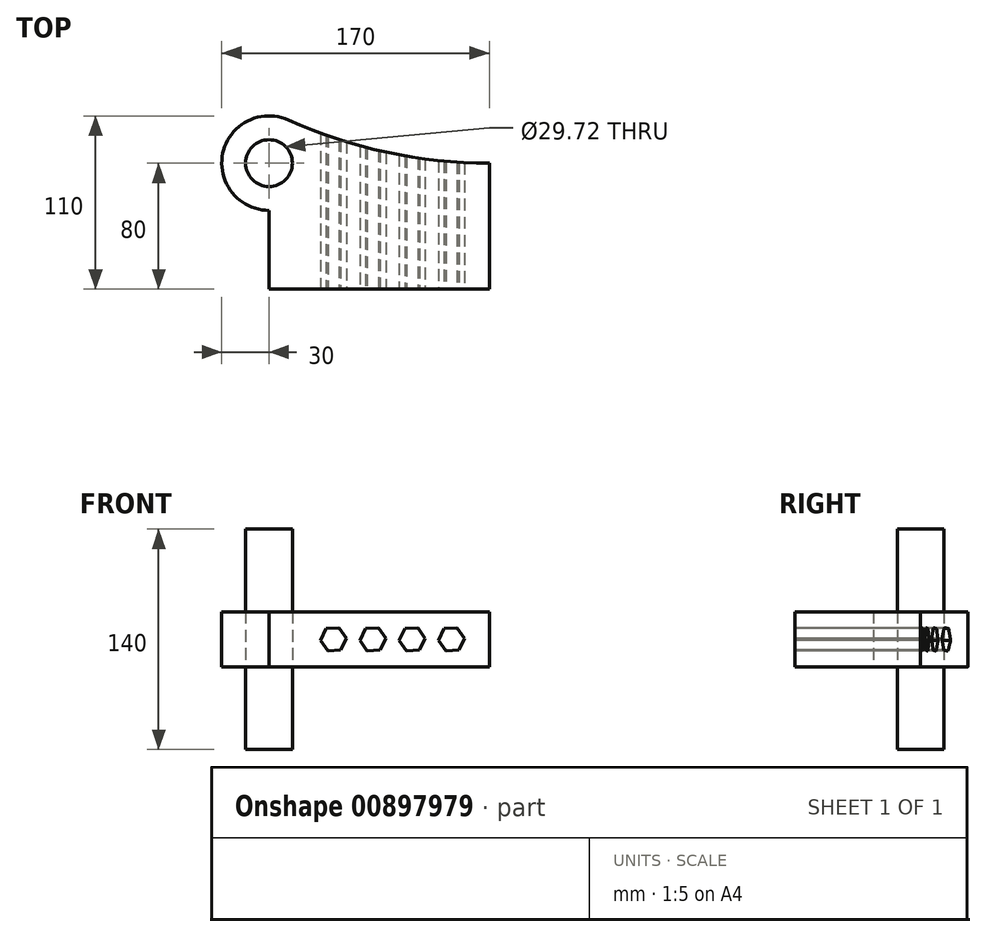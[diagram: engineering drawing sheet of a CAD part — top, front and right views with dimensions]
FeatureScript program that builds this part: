
annotation { "Feature Type Name" : "Feature", "Feature Type Description" : "" }
export const myFeature = defineFeature(function(context is Context, id is Id, definition is map)
    precondition{}
    {
        {
            var Q0;
            Q0=qCreatedBy(makeId("Top.planeOp"),FACE);
            var sketch = newSketch(context, id + "F0", { "sketchPlane" : qUnion([Q0])});
            skLineSegment(sketch, "E0.bottom", {"start": v(70, -40) * mm, "end": v(-70, -40) * mm});
            skLineSegment(sketch, "E0.top", {"start": v(70, 40) * mm, "end": v(-70, 40) * mm});
            skLineSegment(sketch, "E0.left", {"start": v(70, -40) * mm, "end": v(70, 40) * mm});
            skLineSegment(sketch, "E0.right", {"start": v(-70, -40) * mm, "end": v(-70, 40) * mm});
            skPoint(sketch, "E0.middle", {"position": v(0, 0) * mm});
            skCircle(sketch, "E1", {"center": v(-70, 40) * mm, "radius": 30 * mm});
            skArc(sketch, "E2", {"start": v(-57.7, 67.37) * mm, "mid": v(4.7, 46.92) * mm, "end": v(70, 40) * mm});
            skCircle(sketch, "E3", {"center": v(-70, 40) * mm, "radius": 14.86 * mm});
            skSolve(sketch);
        }
        {
            var Q0;
            Q0 = qSketchRegion(id + "F0", true);
            extrude(context, id + "F1", {"entities" : qUnion([Q0]), "endBound" : BoundingType.SYMMETRIC, "depth" : 35 * mm, "offsetDistance" : 25 * mm});
        }
        {
            var Q0;
            {var subQ0=sQuery(id+"F0.wireOp",EDGE,"E0.right");var subQ1=sQuery(id+"F0.wireOp",EDGE,"E0.top");var subQ2=makeQuery(id+"F0.imprint","INTERSECT",VERTEX,{"derivedFrom":[subQ1,subQ0]});Q0=makeQuery(id+"F0.imprint","IMPRINT",FACE,{"disambiguationData":[TD([[makeQuery(id+"F0.imprint","IMPRINT",EDGE,{"disambiguationData":[TD([[subQ2,1.0]])],"derivedFrom":subQ1}),-1.0]])]});}
            var Q1;
            {var subQ0=sQuery(id+"F0.wireOp",EDGE,"E0.right");var subQ1=sQuery(id+"F0.wireOp",EDGE,"E0.top");var subQ2=makeQuery(id+"F0.imprint","INTERSECT",VERTEX,{"derivedFrom":[subQ1,subQ0]});Q1=makeQuery(id+"F0.imprint","IMPRINT",FACE,{"disambiguationData":[TD([[makeQuery(id+"F0.imprint","IMPRINT",EDGE,{"disambiguationData":[TD([[subQ2,1.0]])],"derivedFrom":subQ1}),1.0]])]});}
            extrude(context, id + "F2", {"entities" : qUnion([Q0, Q1]), "endBound" : BoundingType.SYMMETRIC, "depth" : 140 * mm, "offsetDistance" : 25 * mm});
        }
        {
            var Q0;
            Q0=makeQuery(id+"F1.opExtrude","SWEPT_FACE",FACE,{"disambiguationData":[OSD([sQuery(id+"F0.wireOp",EDGE,"E0.bottom")])]});
            var sketch = newSketch(context, id + "F3", { "sketchPlane" : qUnion([Q0])});
            skCircle(sketch, "E4.cCircle", {"center": v(-29.05, 0) * mm, "radius": 8.24 * mm, "construction": true});
            skLineSegment(sketch, "E4.0", {"start": v(-24.41, -6.81) * mm, "end": v(-32.63, -7.42) * mm});
            skLineSegment(sketch, "E4.1", {"start": v(-32.63, -7.42) * mm, "end": v(-37.27, -0.61) * mm});
            skLineSegment(sketch, "E4.2", {"start": v(-37.27, -0.61) * mm, "end": v(-33.69, 6.81) * mm});
            skLineSegment(sketch, "E4.3", {"start": v(-33.69, 6.81) * mm, "end": v(-25.47, 7.42) * mm});
            skLineSegment(sketch, "E4.4", {"start": v(-25.47, 7.42) * mm, "end": v(-20.83, 0.61) * mm});
            skLineSegment(sketch, "E4.5", {"start": v(-20.83, 0.61) * mm, "end": v(-24.41, -6.81) * mm});
            skLineSegment(sketch, "E5.1.0.0", {"start": v(-8.69, 6.81) * mm, "end": v(-0.47, 7.42) * mm});
            skLineSegment(sketch, "E5.1.0.1", {"start": v(-12.27, -0.61) * mm, "end": v(-8.69, 6.81) * mm});
            skLineSegment(sketch, "E5.1.0.2", {"start": v(-7.63, -7.42) * mm, "end": v(-12.27, -0.61) * mm});
            skLineSegment(sketch, "E5.1.0.3", {"start": v(0.59, -6.81) * mm, "end": v(-7.63, -7.42) * mm});
            skLineSegment(sketch, "E5.1.0.4", {"start": v(4.17, 0.61) * mm, "end": v(0.59, -6.81) * mm});
            skLineSegment(sketch, "E5.1.0.5", {"start": v(-0.47, 7.42) * mm, "end": v(4.17, 0.61) * mm});
            skLineSegment(sketch, "E5.2.0.0", {"start": v(16.31, 6.81) * mm, "end": v(24.53, 7.42) * mm});
            skLineSegment(sketch, "E5.2.0.1", {"start": v(12.73, -0.61) * mm, "end": v(16.31, 6.81) * mm});
            skLineSegment(sketch, "E5.2.0.2", {"start": v(17.37, -7.42) * mm, "end": v(12.73, -0.61) * mm});
            skLineSegment(sketch, "E5.2.0.3", {"start": v(25.59, -6.81) * mm, "end": v(17.37, -7.42) * mm});
            skLineSegment(sketch, "E5.2.0.4", {"start": v(29.17, 0.61) * mm, "end": v(25.59, -6.81) * mm});
            skLineSegment(sketch, "E5.2.0.5", {"start": v(24.53, 7.42) * mm, "end": v(29.17, 0.61) * mm});
            skLineSegment(sketch, "E5.3.0.0", {"start": v(41.31, 6.81) * mm, "end": v(49.53, 7.42) * mm});
            skLineSegment(sketch, "E5.3.0.1", {"start": v(37.73, -0.61) * mm, "end": v(41.31, 6.81) * mm});
            skLineSegment(sketch, "E5.3.0.2", {"start": v(42.37, -7.42) * mm, "end": v(37.73, -0.61) * mm});
            skLineSegment(sketch, "E5.3.0.3", {"start": v(50.59, -6.81) * mm, "end": v(42.37, -7.42) * mm});
            skLineSegment(sketch, "E5.3.0.4", {"start": v(54.17, 0.61) * mm, "end": v(50.59, -6.81) * mm});
            skLineSegment(sketch, "E5.3.0.5", {"start": v(49.53, 7.42) * mm, "end": v(54.17, 0.61) * mm});
            skLineSegment(sketch, "E5.direction1", {"start": v(-33.69, 6.81) * mm, "end": v(-8.69, 6.81) * mm, "construction": true});
            skSolve(sketch);
        }
        {
            var Q0;
            Q0=makeQuery(id+"F3.imprint","IMPRINT",FACE,{"disambiguationData":[TD([[makeQuery(id+"F3.imprint","IMPRINT",EDGE,{"derivedFrom":sQuery(id+"F3.wireOp",EDGE,"E5.2.0.0")}),-1.0]])]});
            var Q1;
            Q1=makeQuery(id+"F3.imprint","IMPRINT",FACE,{"disambiguationData":[TD([[makeQuery(id+"F3.imprint","IMPRINT",EDGE,{"derivedFrom":sQuery(id+"F3.wireOp",EDGE,"E5.3.0.0")}),-1.0]])]});
            var Q2;
            Q2=makeQuery(id+"F3.imprint","IMPRINT",FACE,{"disambiguationData":[TD([[makeQuery(id+"F3.imprint","IMPRINT",EDGE,{"derivedFrom":sQuery(id+"F3.wireOp",EDGE,"E5.1.0.0")}),-1.0]])]});
            var Q3;
            Q3=makeQuery(id+"F3.imprint","IMPRINT",FACE,{"disambiguationData":[TD([[makeQuery(id+"F3.imprint","IMPRINT",EDGE,{"derivedFrom":sQuery(id+"F3.wireOp",EDGE,"E4.0")}),-1.0]])]});
            extrude(context, id + "F4", {"entities" : qUnion([Q0, Q1, Q2, Q3]), "operationType" : NewBodyOperationType.REMOVE, "endBound" : BoundingType.THROUGH_ALL, "oppositeDirection" : true, "depth" : 25 * mm, "offsetDistance" : 25 * mm});
        }
    });
